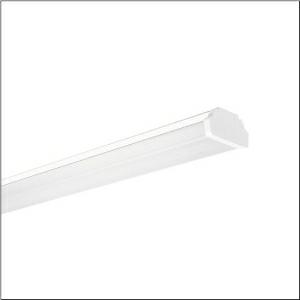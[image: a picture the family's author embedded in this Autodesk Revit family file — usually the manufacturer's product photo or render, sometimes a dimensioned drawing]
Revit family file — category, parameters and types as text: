
# Revit family: dus_31_gen_2_53bd812mv4fxd2_7d94
name_source: partatom
category: Lighting Fixtures
units: mm (PartAtom-declared; Revit-internal decimal feet)

## family parameters
Cut with Voids When Loaded = No
Host = Face
Light Source = No
Part Type = Normal
Room Calculation Point = No
Round Connector Dimension = Use Diameter
Shared = No

## types (1)
- --- (1 x LED, 15440 lm, 82.3 W, 4000K)
    Apparent Load = 82 VA
    CIE Flux Codes = 47 80 95 93 100
    Color Rendering = 80
    Color Temperature = 4000K
    Default Elevation = 1800 mm
    Description = DUS 31 Gen.2, luminaire insert, of sheet steel, coil coated, white, length: 1.535mm, width: 81mm, height: 90mm, 5x system unit, system units: 307mm, LED rated luminous flux: 15.440lm, light colour: 840, SDCM (Standard Deviation of Colour Matching)MacAdam ≤ 3 SDCM (initial), control gear: ON/OFF Multilumen, control gear: ECG, with plug, 3-pole, with phase selection, mains connection: 220..240V, AC, 50/60Hz, rated input power: 82W, through-wiring accessed according to module size, primary optical cover: cover, of PMMA, light emission: direct distribution, primary light characteristic: symmetric, protection rating (complete): IP20, protection rating (LED compartment): IP50, insulation class (complete): insulation class I (protective earthing), certification: CE, ENEC, VDE, UKCA, impact resistance: IK03, permissible ambient temperature for indoor applications: -35..+35°C, corresponds to IFS (International Featured Standards) requirements for safety and quality in the food industry, reducing of maximum allowable ambient temperature of 5°C with ceiling mounting, packaging unit: 1 piece
    Height = 95 mm
    Lamp = 1 x LED
    Lamp Light Flux = 15440 lm
    Lamp Power = 82.3 W
    Lamp count = 1
    Length = 1535 mm
    Luminous efficacy = 188 lm/W
    Manufacturer = Siteco
    ModVariant = No
    Model = 53BD812MV4FXD2
    Mounting Place = Ceiling
    Mounting Type = Pendant
    Number of Poles = 1
    OnlyDefault = Yes
    Power Factor = 1
    Product Name = DUS 31 Gen.2
    Product group = luminaire insert | ceiling pendant
    ProductGroupID = 901
    Protection Class = Protection class I
    Protection Degree = IP 20
    RLX_Detail_Level = 1
    RLX_Emergency_Light_Flux = 0 lm
    RLX_Emergency_Type = 0
    RLX_Emergency_Type_DB = No
    RlxData = <blob elided: 29849 chars, md5=25776f1a>
    Socket = socket
    Standby Power = 0 W
    System Light Flux = 15440 lm
    System Power = 82 W
    Type Comments = factory setting: luminous flux: 100 % | (A | C | E) | 193 mA
    Type Image = l_1319596.jpg
    URL = http://relux.com
    VarID = @adj_049707
    Voltage = 0 V
    Weight = 0.00 kg
    Width = 81 mm

## geometry (parser evidence)
native form markers: Blend x4, Sweep x12
no freeform markers — native parametric forms only
